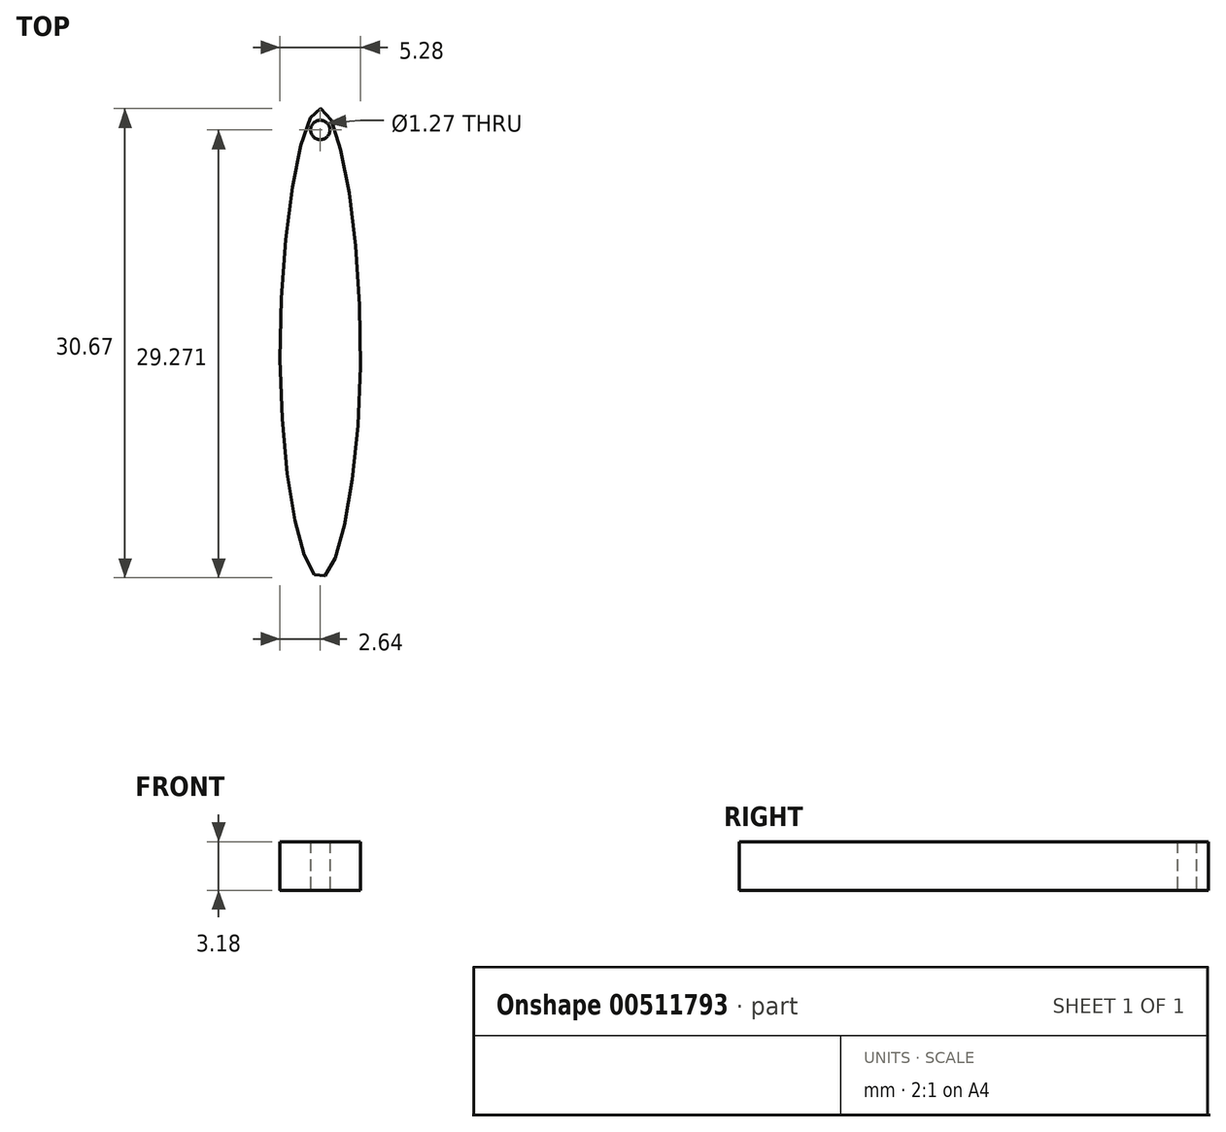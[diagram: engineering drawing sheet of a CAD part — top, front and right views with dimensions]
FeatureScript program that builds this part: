
annotation { "Feature Type Name" : "Feature", "Feature Type Description" : "" }
export const myFeature = defineFeature(function(context is Context, id is Id, definition is map)
    precondition{}
    {
        {
            var Q0;
            Q0=qCreatedBy(makeId("Top.planeOp"),FACE);
            var sketch = newSketch(context, id + "F0", { "sketchPlane" : qUnion([Q0])});
            skFitSpline(sketch, "E0", {"points": [v(-2.64, 0) * mm, v(0, 16.39) * mm, v(2.64, 0) * mm, v(0, -14.28) * mm, v(-2.64, 0) * mm]});
            skPoint(sketch, "E1", {"position": v(0, 15) * mm});
            skSolve(sketch);
        }
        {
            var Q0;
            Q0=makeQuery(id+"F0.imprint","IMPRINT",FACE,{"disambiguationData":[TD([[makeQuery(id+"F0.imprint","IMPRINT",EDGE,{"derivedFrom":sQuery(id+"F0.wireOp",EDGE,"E0")}),-1.0]])]});
            var Q1;
            Q1 = qSketchRegion(id + "F0", true);
            extrude(context, id + "F1", {"entities" : qUnion([Q0, Q1]), "depth" : 3.17 * mm});
        }
        {
            var Q0;
            Q0=sQuery(id+"F0.wireOp",VERTEX,"E1");
            var Q1;
            Q1=makeQuery(id+"F1.opExtrude","SWEPT_BODY",BODY,{"disambiguationData":[OSD([sQuery(id+"F0.wireOp",EDGE,"E0")])]});
            hole(context, id + "F2", {"style" : HoleStyle.SIMPLE, "endStyle" : HoleEndStyle.THROUGH, "oppositeDirection" : true, "holeDiameter" : 1.27 * mm, "isTappedThrough" : true, "tappedDepth" : 12.7 * mm, "tapClearance" : 3, "locations" : qUnion([Q0]), "scope" : qUnion([Q1])});
        }
    });
